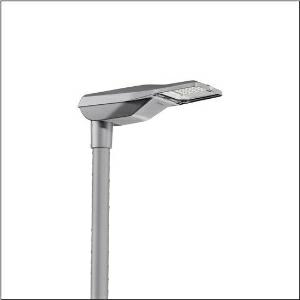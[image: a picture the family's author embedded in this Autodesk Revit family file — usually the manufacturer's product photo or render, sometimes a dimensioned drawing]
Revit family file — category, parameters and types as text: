
# Revit family: streetlight_sl_21_iq_micro___st1_0a_5xe1d61g08cb_d415
name_source: partatom
category: Lighting Fixtures
units: mm (PartAtom-declared; Revit-internal decimal feet)

## family parameters
Cut with Voids When Loaded = No
Host = Face
Light Source = No
Part Type = Normal
Room Calculation Point = No
Round Connector Dimension = Use Diameter
Shared = No

## types (1)
- --- (1 x LED, 2570 lm, 19.4 W, 2700K)
    Apparent Load = 19 VA
    CIE Flux Codes = 37 72 97 100 100
    Color Rendering = 70
    Color Temperature = 2700K
    Default Elevation = 1800 mm
    Description = Streetlight SL 21 iQ micro, mast luminaire, primary light control with lens, of PMMA, primary optical cover: cover, of toughened safety glass, transparent, light distribution: ST1.0a, light emission: direct distribution, primary light characteristic: asymmetric, installation type: post-top, side-entry, LED, High Power LED, rated luminous flux: 2.570lm, luminous efficacy: 133lm/W, light colour: 727, colour temperature: 2700K, control gear: iQ Street-Remote, control: Street-Remote, Auto-Match, Temp-Guard, Lumen-Switch, Night-Set, Smart-Wire, Light-Fading, Desk-Remote (wireless, voltage-free reading and setting of iQ features in the workshop via application-optimized NFC function/RFID function), optimised constant luminous flux control (CLO 2.0), pre-setting: linear dimming characteristic, mains connection: 220..240V, AC, 50/60Hz, start of lifetime: 19W, end of service life: 20W, reduction: 10W, luminaire housing, of diecast aluminium, powder-coated, Siteco® metallic grey (DB 702S), corrosivity category C5 mid according to DIN EN ISO 12944, please order mast flange separately, inclination adjustable: 0°, 5°, 10°, 15°, sealing non-destructively replaceable, multi-level sealing system, length: 528mm, width: 235mm, height: 110mm, mast flange for spigot size: 42mm (side-entry): 5XC10008XM4, 60/48mm (side-entry/post-top): 5XC10108XM2, 76/60mm (side-entry/post-top): 5XC10108XM1, protection rating (complete): IP66, insulation class (complete): insulation class II (safety insulation), certification: CE, ENEC, ENEC+, VDE, impact resistance: IK10, permissible operating ambient temperature for outdoor applications: -40..+50°C, standard-compliant lighting for roads and squares, packaging unit: 1 piece

Light Distribution: ST1.0a
    Height = 110 mm
    Lamp = 1 x LED
    Lamp Light Flux = 2570 lm
    Lamp Power = 19.4 W
    Lamp count = 1
    Length = 528 mm
    Luminous efficacy = 132 lm/W
    Manufacturer = Siteco
    ModVariant = No
    Model = 5XE1D61G08CB
    Number of Poles = 1
    OnlyDefault = Yes
    Power Factor = 1
    Product Name = Streetlight SL 21 iQ micro | ST1.0a
    Product group = mast luminaire | pylon top
    ProductGroupID = 6100
    Protection Class = Protection class II
    Protection Degree = IP 66
    RLX_Detail_Level = 1
    RLX_Emergency_Light_Flux = 0 lm
    RLX_Emergency_Type = 0
    RLX_Emergency_Type_DB = No
    RlxData = <blob elided: 99005 chars, md5=03ff8658>
    Socket = socket
    Standby Power = 0 W
    System Light Flux = 2570 lm
    System Power = 19 W
    Type Comments = factory setting: luminous flux: 100 % | dim-lin: 254 | 387 mA
    Type Image = l_1006881.jpg
    URL = http://relux.com
    VarID = @adj_160587
    Voltage = 0 V
    Weight = 0.00 kg
    Width = 235 mm

## geometry (parser evidence)
native form markers: Blend x4, Sweep x10
no freeform markers — native parametric forms only
